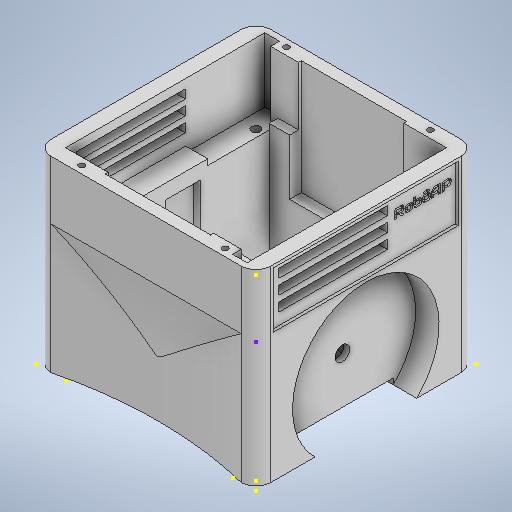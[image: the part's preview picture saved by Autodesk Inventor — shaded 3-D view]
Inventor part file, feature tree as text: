
AUTODESK INVENTOR PART (.ipt)
format: ipt  version: 2025.2 (Build 292293000, 293)  size: 1,241,600 bytes
history: native  units: mm
features: sketch x63, extrude x47, thread x13, other x1
ambient origin geometry x8: Origin, YZ Plane, XZ Plane, XY Plane, X Axis, Y Axis, Z Axis, Center Point
bodies: Body1 (feature_tree)
feature tree (124):
  other  "Sólido1"
  extrude  "Extrusão1"  Depth=75.0mm
  sketch  "Esboço2"  dims[d2=5.0mm d3=5.0mm]
  extrude  "Extrusão2"  Depth=5.0mm
  extrude  "Extrusão3"  Depth=15.0mm TaperAngle=0.0deg
  extrude  "Extrusão4"  Depth=15.0mm TaperAngle=0.0deg
  sketch  "Esboço3"  dims[d4=3.0mm d5=0.0mm d6=15.0mm d7=0.0mm]
  sketch  "Esboço4"  dims[d8=3.0mm d9=0.0mm d10=15.0mm d11=0.0mm]
  extrude  "Extrusão5"  Depth=26.0mm TaperAngle=0.0deg
  extrude  "Extrusão6"  Depth=26.0mm TaperAngle=0.0deg
  sketch  "Esboço7"  dims[d20=65.0mm d21=0.0mm d22=26.0mm d23=0.0mm]
  extrude  "Extrusão7"  Depth=26.0mm TaperAngle=0.0deg
  extrude  "Extrusão8"  Depth=65.0mm TaperAngle=0.0deg
  extrude  "Extrusão9"  Depth=8.0mm TaperAngle=0.0deg
  sketch  "Esboço13"  dims[d33=10.0mm d34=0.0mm d35=5.0mm]
  sketch  "Esboço14"  dims[d36=8.0mm d37=0.0mm d38=10.0mm d39=0.0mm]
  extrude  "Extrusão11"  Depth=5.0mm
  extrude  "Extrusão12"  Depth=10.0mm TaperAngle=0.0deg
  extrude  "Extrusão13"  Depth=6.0mm
  extrude  "Extrusão14"  TaperAngle=180.0deg  [1 undecoded]
  sketch  "Esboço16"  dims[d45=6.0mm d46=180.0deg]
  extrude  "Extrusão15"  TaperAngle=90.0deg  [1 undecoded]
  extrude  "Extrusão16"  Depth=5.0mm
  sketch  "Esboço17"  dims[d47=9.0mm d48=90.0deg]
  extrude  "Extrusão17"  Depth=13.0mm TaperAngle=0.0deg
  extrude  "Extrusão18"  Depth=55.0mm
  sketch  "Esboço20"  dims[d55=3.0mm d56=55.0mm]
  extrude  "Extrusão19"  Depth=13.0mm TaperAngle=0.0deg
  extrude  "Extrusão20"  Depth=24.0mm
  sketch  "Esboço23"  dims[d63=13.0mm d64=0.0mm d65=3.0mm d66=0.0mm]
  extrude  "Extrusão21"  Depth=3.0mm TaperAngle=0.0deg
  extrude  "Extrusão22"  Depth=4.0mm
  sketch  "Esboço26"  dims[d72=90.0deg d73=3.0mm d74=3.0mm d75=3.0mm d76=3.0mm d77=10.0mm d78=0.0mm]
  extrude  "Extrusão23"  Depth=4.0mm
  extrude  "Extrusão24"  Depth=3.0mm
  thread  "Rosca1"  [1 undecoded]
  thread  "Rosca2"  [1 undecoded]
  thread  "Rosca3"  [1 undecoded]
  thread  "Rosca4"  [1 undecoded]
  extrude  "Extrusão25"  Depth=10.0mm TaperAngle=0.0deg
  sketch  "Esboço30"  dims[d90=65.0mm d91=20.0mm d92=0.0mm]
  extrude  "Extrusão26"  Depth=10.0mm TaperAngle=0.0deg
  sketch  "Esboço32"  dims[d95=59.0mm d96=90.0deg]
  extrude  "Extrusão27"  Depth=65.0mm
  sketch  "Esboço34"  dims[d100=39.0mm d101=0.0mm d102=2.0mm d103=0.0mm]
  extrude  "Extrusão28"  Depth=20.0mm TaperAngle=0.0deg
  sketch  "Esboço36"  dims[d112=5.0mm d113=5.0mm d114=5.0mm d115=5.0mm d116=5.0mm d117=44.0mm d118=0.0mm]
  sketch  "Esboço37"  dims[d119=3.0mm d120=3.0mm]
  sketch  "Esboço38"  dims[d121=3.0mm d122=3.0mm]
  extrude  "Extrusão29"  Depth=36.0mm
  extrude  "Extrusão30"  TaperAngle=90.0deg  [1 undecoded]
  extrude  "Extrusão31"  Depth=19.0mm TaperAngle=0.0deg
  sketch  "Esboço41"  dims[d133=8.0mm d134=2.5mm]
  extrude  "Extrusão32"  Depth=2.0mm TaperAngle=0.0deg
  extrude  "Extrusão33"  Depth=63.0mm
  thread  "Rosca5"  [1 undecoded]
  thread  "Rosca6"  [1 undecoded]
  thread  "Rosca7"  [1 undecoded]
  thread  "Rosca8"  [1 undecoded]
  extrude  "Extrusão34"  Depth=5.0mm
  thread  "Rosca9"  [1 undecoded]
  thread  "Rosca10"  [1 undecoded]
  thread  "Rosca11"  [1 undecoded]
  thread  "Rosca12"  [1 undecoded]
  extrude  "Extrusão35"  Depth=3.0mm
  extrude  "Extrusão36"  Depth=3.0mm
  sketch  "Esboço47"  dims[d147=11.0mm d148=0.0mm d149=11.0mm d150=0.0mm]
  sketch  "Esboço48"  dims[d151=11.0mm d152=0.0mm d153=1.0mm]
  sketch  "Esboço49"  dims[d154=1.0mm d155=0.0mm d156=1.0mm d157=0.0mm]
  sketch  "Esboço50"  dims[d171=2.5mm d172=2.5mm]
  sketch  "Esboço51"  dims[d173=16.0mm]
  sketch  "Esboço52"  dims[d177=44.0mm d178=0.0mm]
  sketch  "Esboço53"  dims[d179=10.0mm d180=0.0mm]
  extrude  "Extrusão37"  Depth=10.0mm TaperAngle=0.0deg
  extrude  "Extrusão38"  Depth=11.0mm TaperAngle=0.0deg
  thread  "Rosca13"  [1 undecoded]
  extrude  "Extrusão39"  Depth=2.5mm
  sketch  "Esboço56"  dims[d189=5.0mm d190=0.0mm]
  sketch  "Esboço58"  dims[d193=2.0mm d194=0.0mm]
  extrude  "Extrusão40"  Depth=2.5mm
  extrude  "Extrusão42"  Depth=8.0mm
  extrude  "Extrusão43"  Depth=2.0mm
  sketch  "Esboço60"  dims[d197=2.0mm d198=0.0mm]
  sketch  "Esboço61"  dims[d199=22.0mm d200=0.0mm]
  extrude  "Extrusão44"  Depth=2.0mm
  extrude  "Extrusão45"  Depth=10.0mm TaperAngle=0.0deg
  extrude  "Extrusão46"  Depth=11.0mm TaperAngle=0.0deg
  sketch  "Esboço65"  dims[d211=2.0mm d212=0.0mm]
  extrude  "Extrusão47"  Depth=1.0mm
  sketch  "Esboço69"  dims[d228=1.9mm]
  extrude  "Extrusão48"  Depth=1.0mm TaperAngle=0.0deg
  extrude  "Extrusão49"  Depth=2.5mm
  sketch  "Esboço1"  dims[d0=75.0mm d1=75.0mm]
  sketch  "Esboço5"  dims[d12=50.0mm d13=26.0mm d14=0.0mm]
  sketch  "Esboço6"  dims[d15=26.0mm d16=0.0mm d18=26.0mm d19=0.0mm]
  sketch  "Esboço8"  dims[d26=26.0mm d27=0.0mm d28=65.0mm d29=0.0mm]
  sketch  "Esboço9"  dims[d30=5.0mm d31=8.0mm d32=0.0mm]
  sketch  "Esboço15"  dims[d40=2.0mm d44=6.0mm]
  sketch  "Esboço18"  dims[d49=55.0mm d50=0.0mm d51=5.0mm]
  sketch  "Esboço19"  dims[d52=5.0mm d53=13.0mm d54=0.0mm]
  sketch  "Esboço21"  dims[d57=3.0mm d58=13.0mm d59=0.0mm]
  sketch  "Esboço22"  dims[d60=41.0mm d61=0.0mm d62=24.0mm]
  sketch  "Esboço24"  dims[d67=3.0mm d68=0.0mm d69=4.0mm]
  sketch  "Esboço25"  dims[d70=4.0mm d71=4.0mm]
  sketch  "Esboço27"  dims[d79=10.0mm d80=0.0mm d81=10.0mm d82=0.0mm]
  sketch  "Esboço28"  dims[d83=10.0mm d84=0.0mm d85=10.0mm d86=0.0mm]
  sketch  "Esboço29"  dims[d87=13.0mm d88=0.0mm d89=65.0mm]
  sketch  "Esboço31"  dims[d93=9.5mm d94=36.0mm]
  sketch  "Esboço33"  dims[d97=36.0mm d98=19.0mm d99=0.0mm]
  sketch  "Esboço35"  dims[d104=1.0mm d105=63.0mm d106=1.0mm d107=0.0mm d108=0.0mm d109=0.0mm d110=5.0mm d111=90.0deg]
  sketch  "Esboço39"  dims[d123=10.0mm d124=0.0mm d125=11.0mm d126=0.0mm]
  sketch  "Esboço40"  dims[d127=11.0mm d128=0.0mm d129=11.0mm d130=0.0mm d131=11.0mm d132=0.0mm]
  sketch  "Esboço42"  dims[d135=8.0mm d136=2.5mm]
  sketch  "Esboço43"  dims[d137=2.5mm d138=8.0mm]
  sketch  "Esboço44"  dims[d139=2.0mm d140=2.0mm]
  sketch  "Esboço45"  dims[d141=2.0mm d142=2.0mm]
  sketch  "Esboço46"  dims[d143=10.0mm d144=0.0mm d145=11.0mm d146=0.0mm]
  sketch  "Esboço54"  dims[d181=11.0mm d182=0.0mm]
  sketch  "Esboço55"  dims[d183=28.0mm d184=0.0mm]
  sketch  "Esboço59"  dims[d195=22.0mm d196=0.0mm]
  sketch  "Esboço62"  dims[d201=2.0mm d202=0.0mm]
  sketch  "Esboço68"  dims[d227=1.9mm]
  sketch  "Esboço70"  dims[d229=4.0mm d230=0.0mm]
  sketch  "Esboço71"  dims[d231=14.0mm d232=0.0mm d24=0.5mm d25=0.872665mm d158=0.5mm d159=0.872665mm d160=0.5mm d161=0.872665mm d174=0.5mm d175=0.872665mm d176=0.5mm]
note: 16 required parameter values undecoded (feature->parameter linkage not recoverable at this tier; creation-order binding heuristic only, values carry confidence <= 0.55)
